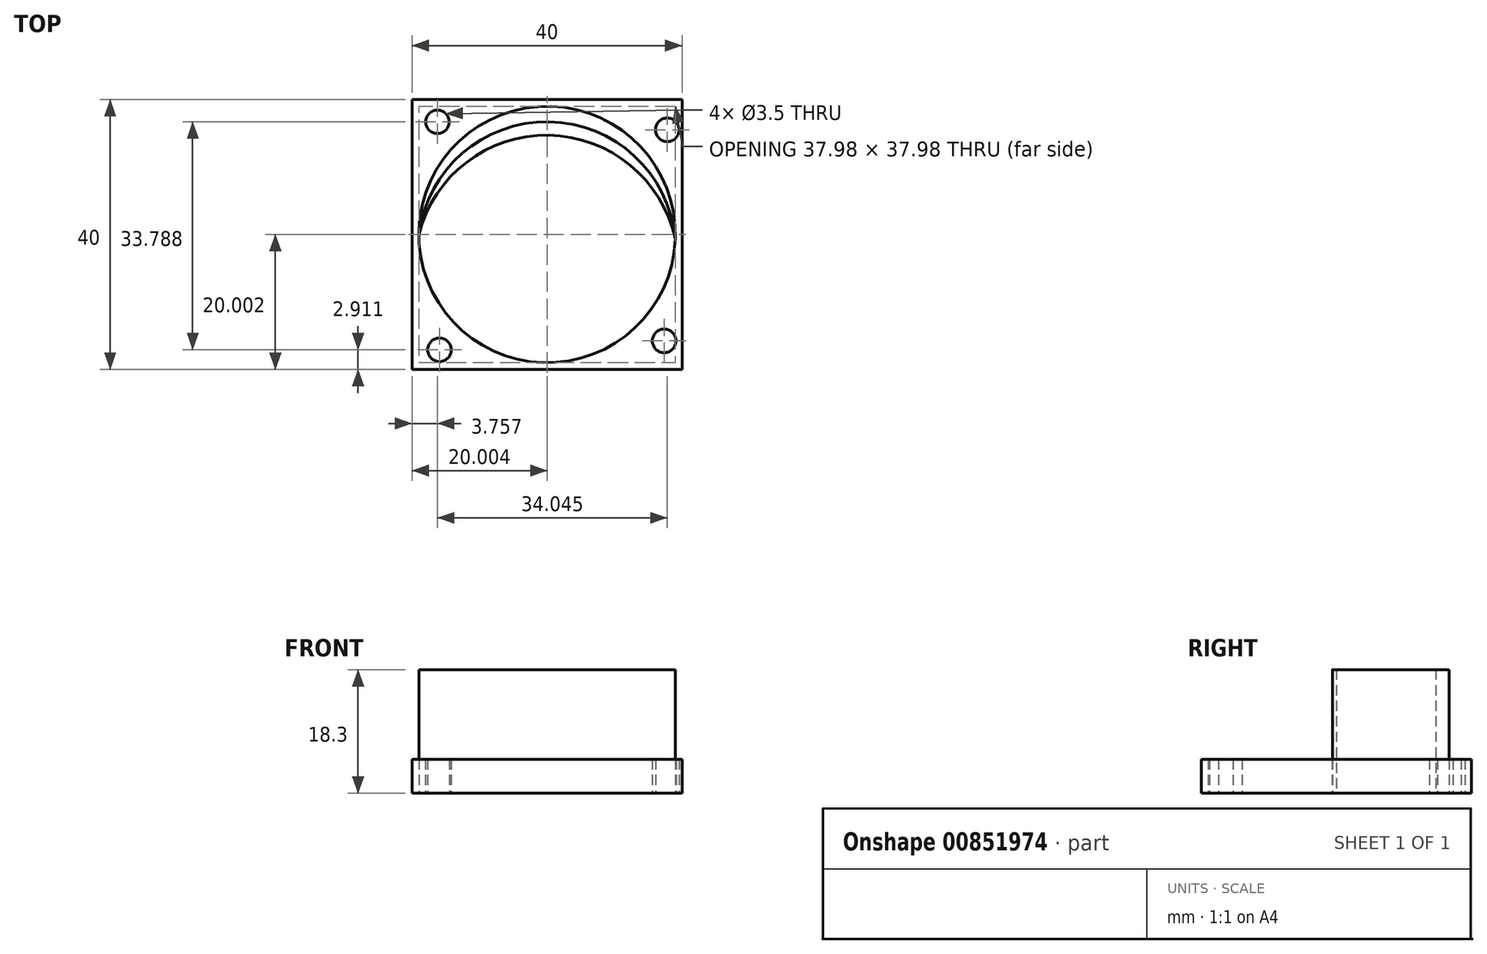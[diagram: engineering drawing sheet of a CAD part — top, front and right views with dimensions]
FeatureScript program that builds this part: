
annotation { "Feature Type Name" : "Feature", "Feature Type Description" : "" }
export const myFeature = defineFeature(function(context is Context, id is Id, definition is map)
    precondition{}
    {
        {
            var Q0;
            Q0=qCreatedBy(makeId("Top.planeOp"),FACE);
            var sketch = newSketch(context, id + "F0", { "sketchPlane" : qUnion([Q0])});
            skLineSegment(sketch, "E0.bottom", {"start": v(-37.4, 18.61) * mm, "end": v(2.6, 18.61) * mm});
            skLineSegment(sketch, "E0.top", {"start": v(-37.4, -21.39) * mm, "end": v(2.6, -21.39) * mm});
            skLineSegment(sketch, "E0.left", {"start": v(-37.4, 18.61) * mm, "end": v(-37.4, -21.39) * mm});
            skLineSegment(sketch, "E0.right", {"start": v(2.6, 18.61) * mm, "end": v(2.6, -21.39) * mm});
            skCircle(sketch, "E1", {"center": v(0.4, 14.12) * mm, "radius": 1.75 * mm});
            skCircle(sketch, "E2", {"center": v(-33.65, 15.3) * mm, "radius": 1.75 * mm});
            skCircle(sketch, "E3", {"center": v(-0.07, -17.15) * mm, "radius": 1.75 * mm});
            skCircle(sketch, "E4", {"center": v(-33.34, -18.48) * mm, "radius": 1.75 * mm});
            skCircle(sketch, "E5", {"center": v(-17.4, -1.39) * mm, "radius": 19 * mm});
            skArc(sketch, "E6", {"start": v(1.59, -2.03) * mm, "mid": v(-17.16, 13.32) * mm, "end": v(-36.4, -1.39) * mm});
            skPoint(sketch, "E7", {"position": v(-37.4, -1.39) * mm});
            skArc(sketch, "E8", {"start": v(1.59, -2.03) * mm, "mid": v(-17.13, 15.32) * mm, "end": v(-36.4, -1.39) * mm});
            skSolve(sketch);
        }
        {
            var Q0;
            Q0 = qSketchRegion(id + "F0", true);
            extrude(context, id + "F1", {"entities" : qUnion([Q0]), "depth" : 5 * mm, "offsetDistance" : 25 * mm});
        }
        {
            var Q0;
            {var subQ0=sQuery(id+"F0.wireOp",EDGE,"E6");var subQ1=sQuery(id+"F0.wireOp",EDGE,"E5");var subQ3=makeQuery(id+"F0.imprint","INTERSECT",VERTEX,{"derivedFrom":[subQ1,subQ0]});Q0=makeQuery(id+"F0.imprint","IMPRINT",FACE,{"disambiguationData":[TD([[makeQuery(id+"F0.imprint","IMPRINT",EDGE,{"disambiguationData":[TD([[subQ3,-1.0]])],"derivedFrom":subQ1}),1.0]])]});}
            extrude(context, id + "F2", {"entities" : qUnion([Q0]), "depth" : 18.3 * mm, "offsetDistance" : 25 * mm});
        }
    });
